# Revit family: Plymold-Contour-Wall_Unit
name_source: partatom
category: Furniture
units: mm (PartAtom-declared; Revit-internal decimal feet)

## family parameters
Always vertical = Yes
Cut with Voids When Loaded = No
OmniClass Number = 23.40.20.00
OmniClass Title = General Furniture and Specialties
Render Appearance Source = Family Geometry
Room Calculation Point = No
Shared = No
Work Plane-Based = No

## types (16) — shared parameters
Assembly Code = E2020200
Cap Finish = PLY - Plastic Black
Default Elevation = 0"
Depth = 63"
Edege Finish = PLY - Plastic Black
Frame Finish = PLY - Onyx Black Powdercoat
Glide Finish = PLY - Plastic Black
Height = 36"
Keynote = 12500
Manufacturer = Plymold
Product Documentation Link = https://plymold.com
Revit File Built By = https://servex-us.com
Seat Finish = PLY - Wood Mahogany
Support Finish = PLY - Onyx Black Powdercoat
Sustainability = https://plymold.com
Top Finish = PLY - Wood Mahogany
Type Comments = Contour
URL = https://plymold.com

## per-type parameters (varying)
| type | DE | Description | Dist Leg | Dist SU1 | Dist1 | Leg | PVC | TPD | VE | Width |
| CBWL047DE | Yes | Contour Booth Unit w/Bullnose Dur-A-Edge® Table Top - 47"W x 63"D x 36"H | 9 3/4" | 12 1/4" | 28" | No | No | No | No | 47" |
| CBWL042DE | Yes | Contour Booth Unit w/Bullnose Dur-A-Edge® Table Top - 42"W x 63"D x 36"H | 4 3/4" | 12 1/4" | 28" | No | No | No | No | 42" |
| CBWL023DE | Yes | Contour Booth Unit w/Bullnose Dur-A-Edge® Table Top - 23"W x 63"D x 36"H | 3 3/4" | 6 1/4" | 16" | No | No | No | No | 23" |
| CBWL059DE | Yes | Contour Booth Unit w/Bullnose Dur-A-Edge® Table Top - 59"W x 63"D x 36"H | 9 3/4" | 13 1/4" | 28" | Yes | No | No | No | 59" |
| CBWL023VE | No | Contour Booth Unit w/Vinyl Edge Table Top - 23"W x 63"D x 36"H | 3 3/4" | 6 1/4" | 16" | No | No | No | Yes | 23" |
| CBWL023TPD | No | Contour Booth Unit w/Thin Vinyl Edge Profile Dur-A-Edge® Table Top - 23"W x 63"D x 36"H | 3 3/4" | 6 1/4" | 16" | No | No | Yes | No | 23" |
| CBWL023PVC | No | Contour Booth Unit w/PVC Edge Table Top - 23"W x 63"D x 36"H | 3 3/4" | 6 1/4" | 16" | No | Yes | No | No | 23" |
| CBWL042PVC | No | Contour Booth Unit w/PVC Edge Table Top - 42"W x 63"D x 36"H | 4 3/4" | 12 1/4" | 28" | No | Yes | No | No | 42" |
| CBWL042TPD | No | Contour Booth Unit w/Thin Vinyl Edge Profile Dur-A-Edge® Table Top - 42"W x 63"D x 36"H | 4 3/4" | 12 1/4" | 28" | No | No | Yes | No | 42" |
| CBWL042VE | No | Contour Booth Unit w/Vinyl Edge Table Top - 42"W x 63"D x 36"H | 4 3/4" | 12 1/4" | 28" | No | No | No | Yes | 42" |
| CBWL047VE | No | Contour Booth Unit w/Vinyl Edge Table Top - 47"W x 63"D x 36"H | 9 3/4" | 12 1/4" | 28" | No | No | No | Yes | 47" |
| CBWL047TPD | No | Contour Booth Unit w/Thin Vinyl Edge Profile Dur-A-Edge® Table Top - 47"W x 63"D x 36"H | 9 3/4" | 12 1/4" | 28" | No | No | Yes | No | 47" |
| CBWL047PVC | No | Contour Booth Unit w/PVC Edge Table Top - 47"W x 63"D x 36"H | 9 3/4" | 12 1/4" | 28" | No | Yes | No | No | 47" |
| CBWL059TPD | No | Contour Booth Unit w/Thin Vinyl Edge Profile Dur-A-Edge® Table Top - 59"W x 63"D x 36"H | 9 3/4" | 13 1/4" | 28" | Yes | No | Yes | No | 59" |
| CBWL059VE | No | Contour Booth Unit w/Vinyl Edge Table Top - 59"W x 63"D x 36"H | 9 3/4" | 13 1/4" | 28" | Yes | No | No | Yes | 59" |
| CBWL059PVC | No | Contour Booth Unit w/PVC Edge Table Top - 59"W x 63"D x 36"H | 9 3/4" | 13 1/4" | 28" | Yes | Yes | No | No | 59" |

note: column(s) folded — value = type name in every type: Model

## geometry (parser evidence)
native form markers: Sweep x13
no freeform markers — native parametric forms only
